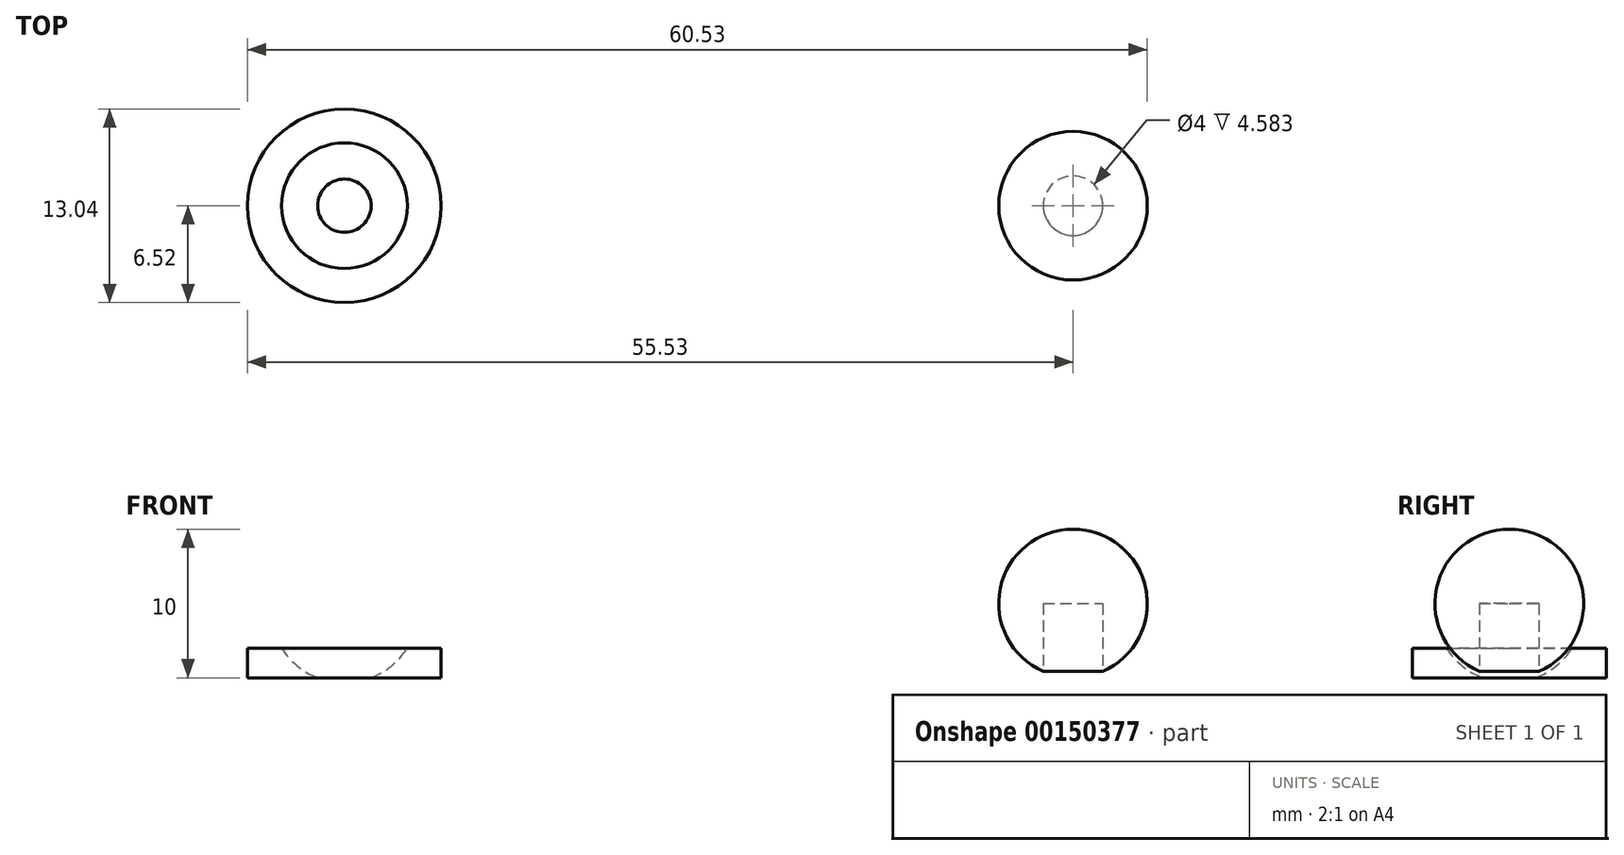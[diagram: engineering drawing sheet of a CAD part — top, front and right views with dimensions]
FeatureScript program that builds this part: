
annotation { "Feature Type Name" : "Feature", "Feature Type Description" : "" }
export const myFeature = defineFeature(function(context is Context, id is Id, definition is map)
    precondition{}
    {
        {
            var Q0;
            Q0=qCreatedBy(makeId("Front.planeOp"),FACE);
            var sketch = newSketch(context, id + "F0", { "sketchPlane" : qUnion([Q0])});
            skLineSegment(sketch, "E0", {"start": v(-2, 0.42) * mm, "end": v(-2, 5) * mm});
            skLineSegment(sketch, "E1", {"start": v(-2, 5) * mm, "end": v(0, 5) * mm});
            skLineSegment(sketch, "E2", {"start": v(0, 5) * mm, "end": v(0, 10) * mm});
            skArc(sketch, "E3", {"start": v(0, 10) * mm, "mid": v(-4.9, 6.02) * mm, "end": v(-2, 0.42) * mm});
            skPoint(sketch, "E4.orphan", {"position": v(-2, 0) * mm});
            skSolve(sketch);
        }
        {
            var Q0;
            Q0 = qSketchRegion(id + "F0", true);
            var Q1;
            Q1=sQuery(id+"F0.wireOp",EDGE,"E2");
            revolve(context, id + "F1", {"entities" : qUnion([Q0]), "axis" : qUnion([Q1]), "revolveType" : RevolveType.FULL});
        }
        {
            var Q0;
            Q0=qCreatedBy(makeId("Front.planeOp"),FACE);
            var sketch = newSketch(context, id + "F2", { "sketchPlane" : qUnion([Q0])});
            skLineSegment(sketch, "E5", {"start": v(-50.8, 0) * mm, "end": v(-55.53, 0) * mm});
            skLineSegment(sketch, "E6", {"start": v(-55.53, 0) * mm, "end": v(-55.53, 2) * mm});
            skArc(sketch, "E7", {"start": v(-53.24, 2) * mm, "mid": v(-52.19, 0.8) * mm, "end": v(-50.8, 0) * mm});
            skLineSegment(sketch, "E8", {"start": v(-49.01, 4.67) * mm, "end": v(-49.01, 0) * mm, "construction": true});
            skLineSegment(sketch, "E9", {"start": v(-55.53, 2) * mm, "end": v(-53.24, 2) * mm});
            skSolve(sketch);
        }
        {
            var Q0;
            Q0 = qSketchRegion(id + "F2", true);
            var Q1;
            Q1=sQuery(id+"F2.wireOp",EDGE,"E8");
            revolve(context, id + "F3", {"entities" : qUnion([Q0]), "axis" : qUnion([Q1]), "revolveType" : RevolveType.FULL});
        }
    });
